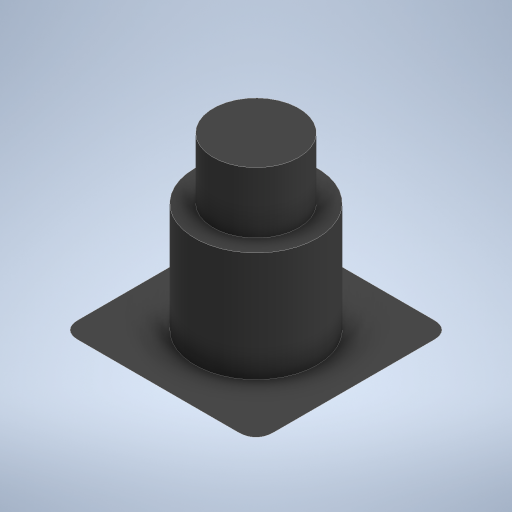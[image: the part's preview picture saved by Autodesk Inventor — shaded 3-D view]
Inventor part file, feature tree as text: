
AUTODESK INVENTOR PART (.ipt)
format: ipt  version: 2024.2 (Build 282272000, 272)  size: 287,232 bytes
history: native  units: mm
features: extrude x4, sketch x4, fillet x2, chamfer x1
ambient origin geometry x8: Origin, YZ Plane, XZ Plane, XY Plane, X Axis, Y Axis, Z Axis, Center Point
bodies: Solid1 (feature_tree)
feature tree (11):
  extrude  "Extrusion1"  Depth=9.0mm TaperAngle=0.0deg
  extrude  "Extrusion2"  Depth=5.0mm TaperAngle=0.0deg
  extrude  "Extrusion3"  Depth=16.0mm
  chamfer  "Chamfer1"  Distance=8.0mm
  fillet  "Fillet1"  Radius=2.0mm
  extrude  "Extrusion4"  Depth=2.0mm TaperAngle=45.0deg
  fillet  "Fillet2"  Radius=2.0mm
  sketch  "Sketch1"  dims[d0=10.0mm d1=9.0mm d2=0.0mm]
  sketch  "Sketch2"  dims[d3=7.0mm d4=5.0mm d5=0.0mm]
  sketch  "Sketch3"  dims[d6=16.0mm d7=16.0mm]
  sketch  "Sketch4"  dims[d8=8.0mm d9=8.0mm d10=2.0mm d11=0.0mm d12=2.0mm d13=2.0mm d14=45.0deg d15=2.0mm d16=9.0mm d17=1.5mm d18=0.0mm d19=0.2mm]
